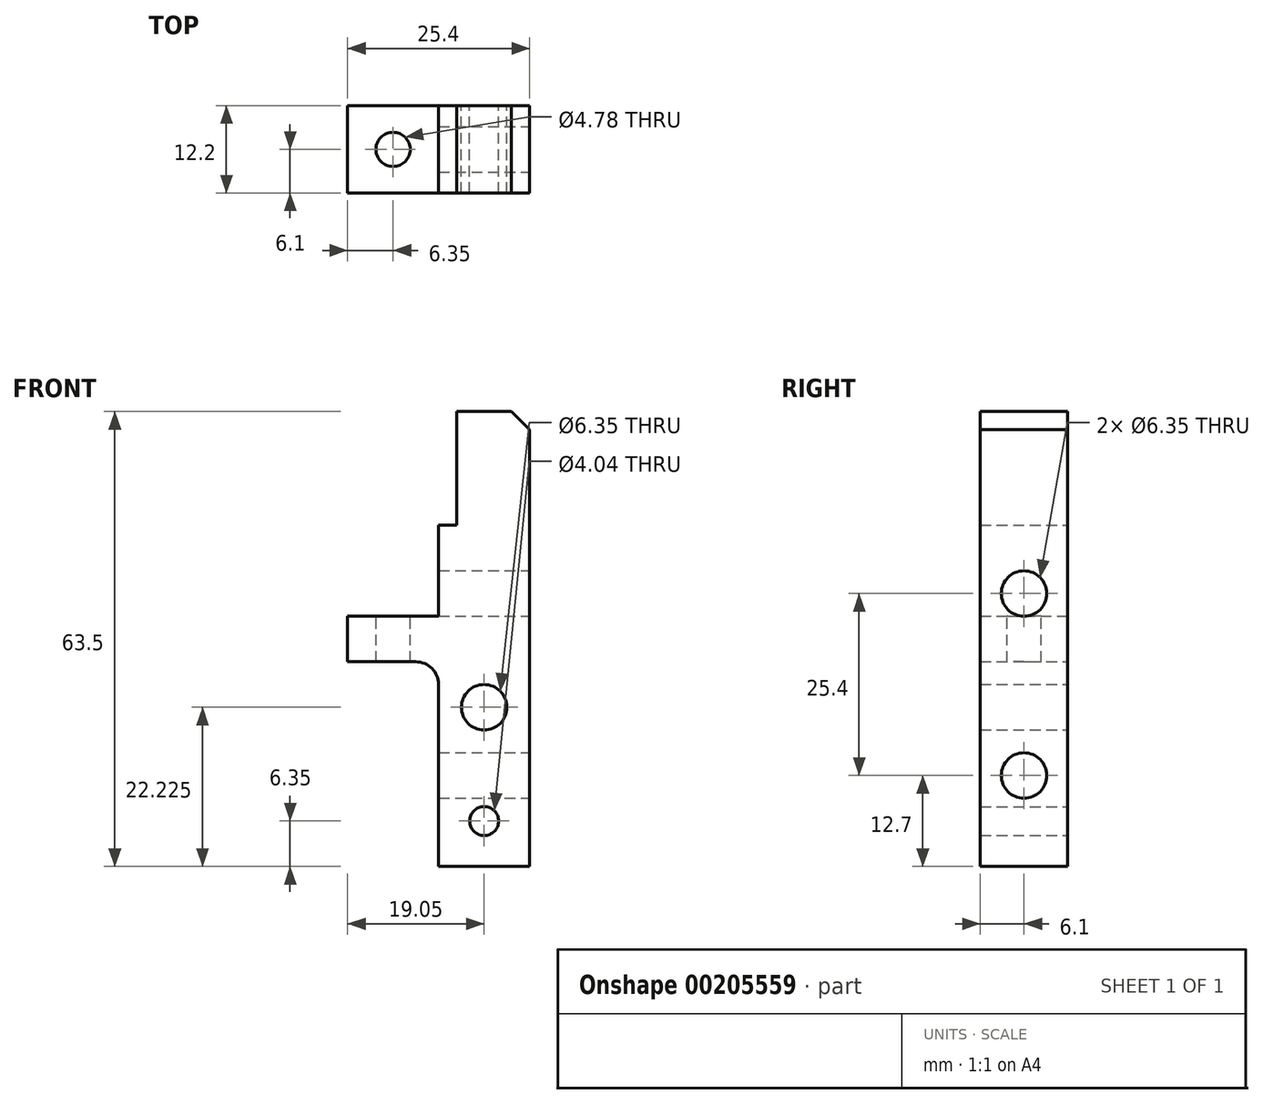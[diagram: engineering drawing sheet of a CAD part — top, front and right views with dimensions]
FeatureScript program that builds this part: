
annotation { "Feature Type Name" : "Feature", "Feature Type Description" : "" }
export const myFeature = defineFeature(function(context is Context, id is Id, definition is map)
    precondition{}
    {
        {
            var Q0;
            Q0=qCreatedBy(makeId("Front.planeOp"),FACE);
            var sketch = newSketch(context, id + "F0", { "sketchPlane" : qUnion([Q0])});
            skLineSegment(sketch, "E0", {"start": v(0, 0) * mm, "end": v(0, -63.5) * mm});
            skLineSegment(sketch, "E1", {"start": v(0, -63.5) * mm, "end": v(-12.7, -63.5) * mm});
            skLineSegment(sketch, "E2", {"start": v(-12.7, -63.5) * mm, "end": v(-12.7, -38.1) * mm});
            skLineSegment(sketch, "E3", {"start": v(-15.87, -34.93) * mm, "end": v(-25.4, -34.93) * mm});
            skLineSegment(sketch, "E4", {"start": v(-25.4, -34.93) * mm, "end": v(-25.4, -28.58) * mm});
            skLineSegment(sketch, "E5", {"start": v(-25.4, -28.58) * mm, "end": v(-12.7, -28.58) * mm});
            skLineSegment(sketch, "E6", {"start": v(-12.7, -28.58) * mm, "end": v(-12.7, -15.88) * mm});
            skLineSegment(sketch, "E7", {"start": v(-12.7, -15.88) * mm, "end": v(-10.16, -15.88) * mm});
            skLineSegment(sketch, "E8", {"start": v(-10.16, -15.88) * mm, "end": v(-10.16, 0) * mm});
            skLineSegment(sketch, "E9", {"start": v(-10.16, 0) * mm, "end": v(0, 0) * mm});
            skPoint(sketch, "E10.visualSharp", {"position": v(-12.7, -34.93) * mm});
            skArc(sketch, "E10.filletArc", {"start": v(-12.7, -38.1) * mm, "mid": v(-13.63, -35.85) * mm, "end": v(-15.87, -34.93) * mm});
            skCircle(sketch, "E11", {"center": v(-6.35, -41.28) * mm, "radius": 3.18 * mm});
            skPoint(sketch, "E12.centerSnap0", {"position": v(-25.4, -31.75) * mm});
            skCircle(sketch, "E13", {"center": v(-6.35, -57.15) * mm, "radius": 2.02 * mm});
            skSolve(sketch);
        }
        {
            var Q0;
            Q0=qSketchRegion(id+"F0",true);
            extrude(context, id + "F1", {"entities" : qUnion([Q0]), "depth" : 12.2 * mm, "symmetric" : true});
        }
        {
            var Q0;
            Q0=makeQuery(id+"F1.opExtrude","SWEPT_FACE",FACE,{"disambiguationData":[OSD([sQuery(id+"F0.wireOp",EDGE,"E0")])]});
            var sketch = newSketch(context, id + "F2", { "sketchPlane" : qUnion([Q0])});
            skCircle(sketch, "E14", {"center": v(0, -25.4) * mm, "radius": 3.17 * mm});
            skCircle(sketch, "E15", {"center": v(0, -50.8) * mm, "radius": 3.18 * mm});
            skSolve(sketch);
        }
        {
            var Q0;
            Q0=qSketchRegion(id+"F2",true);
            extrude(context, id + "F3", {"entities" : qUnion([Q0]), "operationType" : NewBodyOperationType.REMOVE, "endBound" : BoundingType.THROUGH_ALL, "oppositeDirection" : true, "depth" : 25.4 * mm});
        }
        {
            var Q0;
            Q0=makeQuery(id+"F1.opExtrude","SWEPT_FACE",FACE,{"disambiguationData":[OSD([sQuery(id+"F0.wireOp",EDGE,"E5")])]});
            var sketch = newSketch(context, id + "F4", { "sketchPlane" : qUnion([Q0])});
            skCircle(sketch, "E16", {"center": v(-19.05, 0) * mm, "radius": 2.39 * mm});
            skSolve(sketch);
        }
        {
            var Q0;
            Q0=qSketchRegion(id+"F4",true);
            extrude(context, id + "F5", {"entities" : qUnion([Q0]), "operationType" : NewBodyOperationType.REMOVE, "endBound" : BoundingType.THROUGH_ALL, "oppositeDirection" : true, "depth" : 25.4 * mm});
        }
        {
            var Q0;
            Q0=makeQuery(id+"F1.opExtrude","SWEPT_EDGE",EDGE,{"disambiguationData":[OSD([sQuery(id+"F0.wireOp",EDGE,"E0"),sQuery(id+"F0.wireOp",EDGE,"E9")])]});
            chamfer(context, id + "F6", {"entities" : qUnion([Q0]), "width" : 2.54 * mm, "tangentPropagation" : true});
        }
    });
